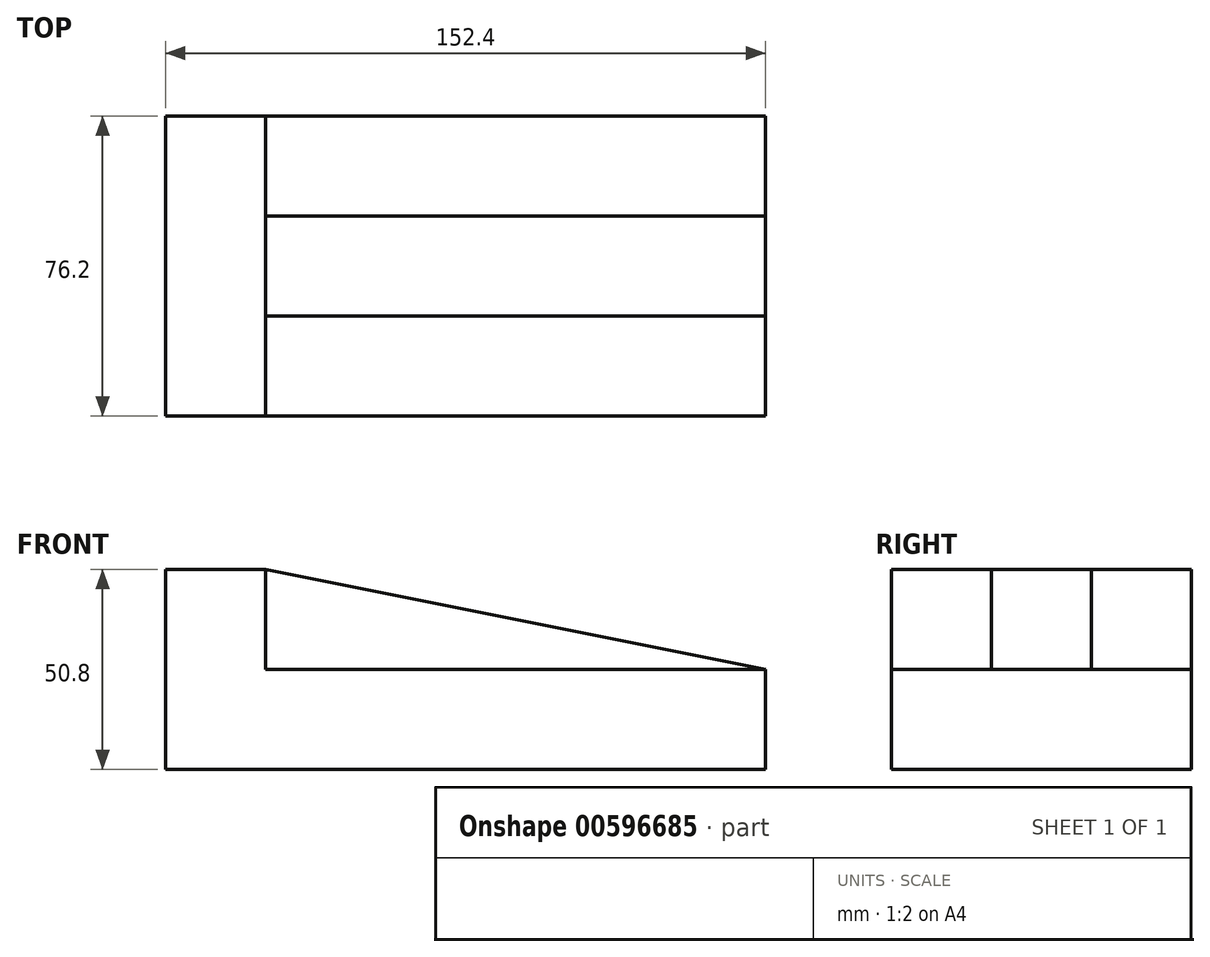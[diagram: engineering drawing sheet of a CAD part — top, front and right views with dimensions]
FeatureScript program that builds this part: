
annotation { "Feature Type Name" : "Feature", "Feature Type Description" : "" }
export const myFeature = defineFeature(function(context is Context, id is Id, definition is map)
    precondition{}
    {
        {
            var Q0;
            Q0=qCreatedBy(makeId("Front.planeOp"),FACE);
            var sketch = newSketch(context, id + "F0", { "sketchPlane" : qUnion([Q0])});
            skLineSegment(sketch, "E0.bottom", {"start": v(0, 0) * mm, "end": v(-152.4, 0) * mm});
            skLineSegment(sketch, "E0.top", {"start": v(0, 50.8) * mm, "end": v(-152.4, 50.8) * mm});
            skLineSegment(sketch, "E0.left", {"start": v(0, 0) * mm, "end": v(0, 50.8) * mm});
            skLineSegment(sketch, "E0.right", {"start": v(-152.4, 0) * mm, "end": v(-152.4, 50.8) * mm});
            skSolve(sketch);
        }
        {
            var Q0;
            Q0=makeQuery(id+"F0.imprint","IMPRINT",FACE,{"disambiguationData":[TD([[makeQuery(id+"F0.imprint","IMPRINT",EDGE,{"derivedFrom":sQuery(id+"F0.wireOp",EDGE,"E0.bottom")}),-1.0]])]});
            extrude(context, id + "F1", {"entities" : qUnion([Q0]), "depth" : 76.2 * mm, "offsetDistance" : 25.4 * mm});
        }
        {
            var Q0;
            Q0=makeQuery(id+"F1.opExtrude","CAP_FACE",FACE,{"disambiguationData":[OSD([sQuery(id+"F0.wireOp",EDGE,"E0.bottom"),sQuery(id+"F0.wireOp",EDGE,"E0.top"),sQuery(id+"F0.wireOp",EDGE,"E0.left"),sQuery(id+"F0.wireOp",EDGE,"E0.right")])],"isStart":false});
            var sketch = newSketch(context, id + "F2", { "sketchPlane" : qUnion([Q0])});
            skLineSegment(sketch, "E1", {"start": v(-152.4, 50.8) * mm, "end": v(-127, 50.8) * mm});
            skLineSegment(sketch, "E2", {"start": v(-127, 50.8) * mm, "end": v(-127, 25.4) * mm});
            skLineSegment(sketch, "E3", {"start": v(-127, 25.4) * mm, "end": v(0, 25.4) * mm});
            skSolve(sketch);
        }
        {
            var Q0;
            {var subQ0=sQuery(id+"F2.wireOp",EDGE,"E2");Q0=makeQuery(id+"F2.imprint","IMPRINT",FACE,{"disambiguationData":[TD([[makeQuery(id+"F2.imprint","IMPRINT",EDGE,{"derivedFrom":subQ0}),1.0]])]});}
            extrude(context, id + "F3", {"entities" : qUnion([Q0]), "operationType" : NewBodyOperationType.REMOVE, "oppositeDirection" : true, "depth" : 97.03 * mm, "offsetDistance" : 25.4 * mm});
        }
        {
            var Q0;
            Q0=makeQuery(id+"F3.boolean.opBoolean","COPY",FACE,{"derivedFrom":makeQuery(id+"F3.opExtrude","SWEPT_FACE",FACE,{"disambiguationData":[OSD([sQuery(id+"F2.wireOp",EDGE,"E2")])]})});
            var sketch = newSketch(context, id + "F4", { "sketchPlane" : qUnion([Q0])});
            skLineSegment(sketch, "E4", {"start": v(-76.2, 50.8) * mm, "end": v(-50.8, 50.8) * mm});
            skLineSegment(sketch, "E5", {"start": v(-50.8, 50.8) * mm, "end": v(-50.8, 25.4) * mm});
            skLineSegment(sketch, "E6", {"start": v(0, 50.8) * mm, "end": v(-25.4, 50.8) * mm});
            skLineSegment(sketch, "E7", {"start": v(-50.8, 50.8) * mm, "end": v(-25.4, 50.8) * mm});
            skLineSegment(sketch, "E8", {"start": v(-50.8, 25.4) * mm, "end": v(-25.4, 25.4) * mm});
            skLineSegment(sketch, "E9", {"start": v(-25.4, 25.4) * mm, "end": v(-25.4, 50.8) * mm});
            skSolve(sketch);
        }
        {
            var Q0;
            Q0=makeQuery(id+"F4.imprint","IMPRINT",FACE,{"disambiguationData":[TD([[makeQuery(id+"F4.imprint","IMPRINT",EDGE,{"derivedFrom":sQuery(id+"F4.wireOp",EDGE,"E5")}),1.0]])]});
            extrude(context, id + "F5", {"entities" : qUnion([Q0]), "operationType" : NewBodyOperationType.ADD, "depth" : 127 * mm, "offsetDistance" : 25.4 * mm});
        }
        {
            var Q0;
            Q0=makeQuery(id+"F5.opExtrude","SWEPT_FACE",FACE,{"disambiguationData":[OSD([sQuery(id+"F4.wireOp",EDGE,"E5")])]});
            var sketch = newSketch(context, id + "F6", { "sketchPlane" : qUnion([Q0])});
            skLineSegment(sketch, "E10", {"start": v(-127, 50.8) * mm, "end": v(0, 25.4) * mm});
            skSolve(sketch);
        }
        {
            var Q0;
            Q0=makeQuery(id+"F6.imprint","IMPRINT",FACE,{"disambiguationData":[TD([[makeQuery(id+"F6.imprint","IMPRINT",EDGE,{"derivedFrom":sQuery(id+"F6.wireOp",EDGE,"E10")}),1.0]])]});
            extrude(context, id + "F7", {"entities" : qUnion([Q0]), "operationType" : NewBodyOperationType.REMOVE, "oppositeDirection" : true, "depth" : 72.64 * mm, "offsetDistance" : 25.4 * mm});
        }
    });
